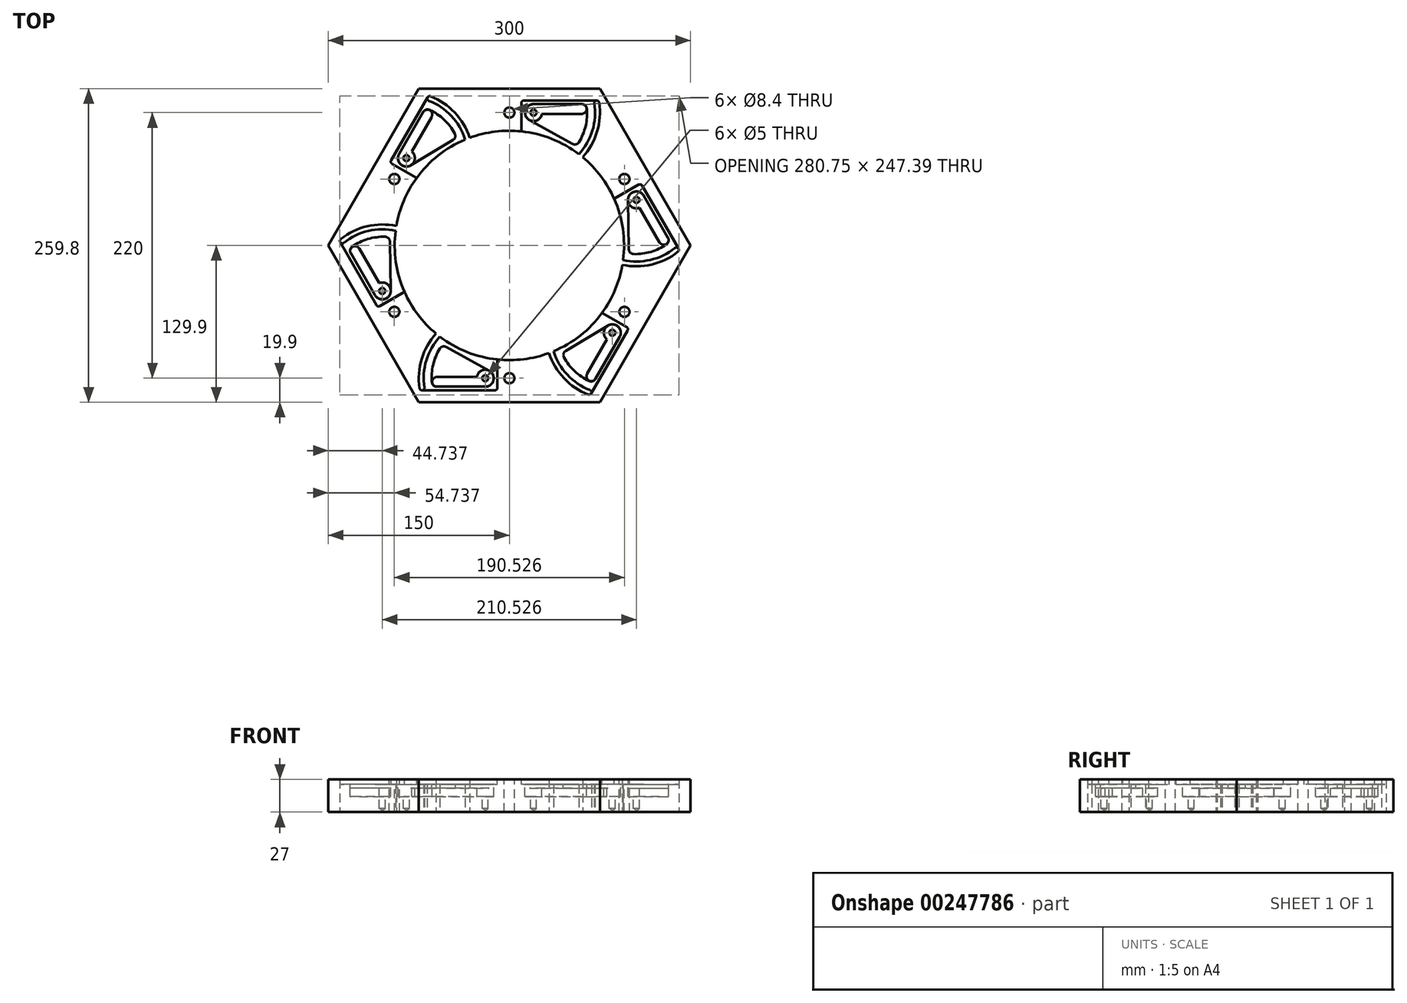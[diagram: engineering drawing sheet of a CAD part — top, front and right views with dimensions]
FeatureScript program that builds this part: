
annotation { "Feature Type Name" : "Feature", "Feature Type Description" : "" }
export const myFeature = defineFeature(function(context is Context, id is Id, definition is map)
    precondition{}
    {
        {
            var Q0;
            Q0=qCreatedBy(makeId("Top.planeOp"),FACE);
            var sketch = newSketch(context, id + "F0", { "sketchPlane" : qUnion([Q0])});
            skCircle(sketch, "E0.cCircle", {"center": v(0, 0) * mm, "radius": 150 * mm, "construction": true});
            skLineSegment(sketch, "E0.0", {"start": v(-75, 129.9) * mm, "end": v(75, 129.9) * mm});
            skLineSegment(sketch, "E0.1", {"start": v(75, 129.9) * mm, "end": v(150, 0) * mm});
            skLineSegment(sketch, "E0.2", {"start": v(150, 0) * mm, "end": v(75, -129.9) * mm});
            skLineSegment(sketch, "E0.3", {"start": v(75, -129.9) * mm, "end": v(-75, -129.9) * mm});
            skLineSegment(sketch, "E0.4", {"start": v(-75, -129.9) * mm, "end": v(-150, 0) * mm});
            skLineSegment(sketch, "E0.5", {"start": v(-150, 0) * mm, "end": v(-75, 129.9) * mm});
            skCircle(sketch, "E1", {"center": v(0, 0) * mm, "radius": 95 * mm});
            skLineSegment(sketch, "E2", {"start": v(0, -192.57) * mm, "end": v(0, 170.24) * mm, "construction": true});
            skCircle(sketch, "E3", {"center": v(0, 0) * mm, "radius": 110 * mm, "construction": true});
            skCircle(sketch, "E4", {"center": v(0, 110) * mm, "radius": 4.2 * mm});
            skCircle(sketch, "E5.1.0", {"center": v(-95.26, 55) * mm, "radius": 4.2 * mm});
            skCircle(sketch, "E5.2.0", {"center": v(-95.26, -55) * mm, "radius": 4.2 * mm});
            skCircle(sketch, "E5.3.0", {"center": v(0, -110) * mm, "radius": 4.2 * mm});
            skCircle(sketch, "E5.4.0", {"center": v(95.26, -55) * mm, "radius": 4.2 * mm});
            skCircle(sketch, "E5.5.0", {"center": v(95.26, 55) * mm, "radius": 4.2 * mm});
            skSolve(sketch);
        }
        {
            var Q0;
            Q0=qSketchRegion(id+"F0",true);
            extrude(context, id + "F1", {"entities" : qUnion([Q0]), "oppositeDirection" : true, "depth" : 25 * mm, "hasSecondDirection" : true, "secondDirectionOppositeDirection" : false, "secondDirectionDepth" : 2 * mm});
        }
        {
            var Q0;
            Q0=qCreatedBy(makeId("Top.planeOp"),FACE);
            var sketch = newSketch(context, id + "F2", { "sketchPlane" : qUnion([Q0])});
            skLineSegment(sketch, "E6", {"start": v(0, 0) * mm, "end": v(-115.33, 66.59) * mm, "construction": true});
            skLineSegment(sketch, "E7", {"start": v(24.73, 8.82) * mm, "end": v(-118.6, 91.57) * mm, "construction": true});
            skLineSegment(sketch, "E8", {"start": v(-73.53, 92.65) * mm, "end": v(-110.35, 28.87) * mm, "construction": true});
            skPoint(sketch, "E9", {"position": v(-85.26, 72.32) * mm});
            skArc(sketch, "E10", {"start": v(-79.2, 122.96) * mm, "mid": v(-97.67, 22.85) * mm, "end": v(-66.72, 119.83) * mm, "construction": true});
            skArc(sketch, "E11", {"start": v(-78.72, 126.93) * mm, "mid": v(-131.29, 42.21) * mm, "end": v(-32.6, 56.43) * mm});
            skCircle(sketch, "E12", {"center": v(-85.26, 72.32) * mm, "radius": 2.5 * mm, "construction": true});
            skArc(sketch, "E13", {"start": v(-86.7, 77.1) * mm, "mid": v(-89.8, 70.21) * mm, "end": v(-82.54, 68.13) * mm, "construction": true});
            skLineSegment(sketch, "E14", {"start": v(-95.36, 62.49) * mm, "end": v(-73.35, 109.7) * mm, "construction": true});
            skArc(sketch, "E15", {"start": v(-86.7, 77.1) * mm, "mid": v(-83.05, 79.12) * mm, "end": v(-80.54, 82.45) * mm, "construction": true});
            skLineSegment(sketch, "E16.trimOffspring", {"start": v(-80.54, 82.45) * mm, "end": v(-62.02, 122.17) * mm, "construction": true});
            skLineSegment(sketch, "E17.trimOffspring", {"start": v(-37.22, 89.44) * mm, "end": v(-33.46, 90.8) * mm});
            skPoint(sketch, "E18", {"position": v(-62.02, 122.17) * mm});
            skPoint(sketch, "E19", {"position": v(-33.46, 90.8) * mm});
            skArc(sketch, "E20", {"start": v(-37.22, 89.44) * mm, "mid": v(-37.91, 91.27) * mm, "end": v(-38.67, 93.07) * mm});
            skLineSegment(sketch, "E21", {"start": v(-82.54, 68.13) * mm, "end": v(-42.49, 94.14) * mm, "construction": true});
            skLineSegment(sketch, "E22", {"start": v(-50.7, 85.23) * mm, "end": v(-31.42, 97.75) * mm, "construction": true});
            skPoint(sketch, "E23", {"position": v(-39.97, 95.77) * mm});
            skCircle(sketch, "E24", {"center": v(-39.97, 95.77) * mm, "radius": 3 * mm, "construction": true});
            skPoint(sketch, "E25", {"position": v(-42.49, 94.14) * mm});
            skArc(sketch, "E26.trimOffspring", {"start": v(-39.97, 95.77) * mm, "mid": v(-49.96, 109.12) * mm, "end": v(-63.7, 118.54) * mm, "construction": true});
            skLineSegment(sketch, "E27.trimOffspring", {"start": v(-39.97, 95.77) * mm, "end": v(-16, 111.34) * mm});
            skArc(sketch, "E28", {"start": v(-38.67, 93.07) * mm, "mid": v(-40.33, 94.5) * mm, "end": v(-42.49, 94.14) * mm});
            skPoint(sketch, "E29", {"position": v(-77.2, 132.91) * mm});
            skPoint(sketch, "E30", {"position": v(-78.72, 126.93) * mm});
            skLineSegment(sketch, "E31", {"start": v(-85.26, 72.32) * mm, "end": v(-78.72, 126.93) * mm, "construction": true});
            skLineSegment(sketch, "E32", {"start": v(-85.21, 72.2) * mm, "end": v(-33.46, 90.8) * mm, "construction": true});
            skPoint(sketch, "E33", {"position": v(-56.33, 130.09) * mm});
            skLineSegment(sketch, "E34", {"start": v(-97.92, 70.4) * mm, "end": v(-67.73, 122.7) * mm});
            skLineSegment(sketch, "E35.1.0", {"start": v(0, 0) * mm, "end": v(-115.33, -66.59) * mm});
            skPoint(sketch, "E35.1.1", {"position": v(-105.26, -37.68) * mm});
            skLineSegment(sketch, "E35.2.0", {"start": v(0, 0) * mm, "end": v(0, -133.17) * mm});
            skPoint(sketch, "E35.2.1", {"position": v(-20, -110) * mm});
            skLineSegment(sketch, "E35.3.0", {"start": v(0, 0) * mm, "end": v(115.33, -66.59) * mm});
            skPoint(sketch, "E35.3.1", {"position": v(85.26, -72.32) * mm});
            skLineSegment(sketch, "E35.4.0", {"start": v(0, 0) * mm, "end": v(115.33, 66.59) * mm});
            skPoint(sketch, "E35.4.1", {"position": v(105.26, 37.68) * mm});
            skLineSegment(sketch, "E35.5.0", {"start": v(0, 0) * mm, "end": v(0, 133.17) * mm});
            skPoint(sketch, "E35.5.1", {"position": v(20, 110) * mm});
            skPoint(sketch, "E35.center", {"position": v(0, 0) * mm});
            skCircle(sketch, "E36.0", {"center": v(0, 0) * mm, "radius": 95 * mm, "construction": true});
            skPoint(sketch, "E37", {"position": v(-32.9, 89.12) * mm});
            skLineSegment(sketch, "E38", {"start": v(-32.9, 89.12) * mm, "end": v(32.9, -89.12) * mm, "construction": true});
            skPoint(sketch, "E39", {"position": v(-22.5, 60.98) * mm});
            skPoint(sketch, "E40", {"position": v(5.2, -14.07) * mm});
            skCircle(sketch, "E41", {"center": v(5.2, -14.07) * mm, "radius": 80 * mm, "construction": true});
            skArc(sketch, "E42.filletArc", {"start": v(-65.27, 123.56) * mm, "mid": v(-66.66, 123.58) * mm, "end": v(-67.73, 122.7) * mm});
            skLineSegment(sketch, "E43", {"start": v(-32.6, 56.43) * mm, "end": v(-85.26, 72.32) * mm, "construction": true});
            skLineSegment(sketch, "E44", {"start": v(-76.12, 72.3) * mm, "end": v(-85.21, 72.2) * mm});
            skLineSegment(sketch, "E45", {"start": v(-85.21, 72.2) * mm, "end": v(-56.33, 90.95) * mm, "construction": true});
            skLineSegment(sketch, "E46", {"start": v(-85.21, 72.2) * mm, "end": v(-48.78, 69.91) * mm, "construction": true});
            skLineSegment(sketch, "E47", {"start": v(-48.77, 65.04) * mm, "end": v(-92.23, 67.76) * mm, "construction": true});
            skCircle(sketch, "E48", {"center": v(-85.21, 72.2) * mm, "radius": 10 * mm, "construction": true});
            skLineSegment(sketch, "E49", {"start": v(-87.5, 62.45) * mm, "end": v(-55.32, 60.44) * mm, "construction": true});
            skLineSegment(sketch, "E50", {"start": v(-97.2, 67.66) * mm, "end": v(-68.1, 50.87) * mm});
            skArc(sketch, "E51.filletArc", {"start": v(-97.92, 70.4) * mm, "mid": v(-98.12, 68.87) * mm, "end": v(-97.2, 67.66) * mm});
            skArc(sketch, "E52", {"start": v(-67.73, 122.7) * mm, "mid": v(-67.88, 121.03) * mm, "end": v(-66.72, 119.83) * mm, "construction": true});
            skArc(sketch, "E53.converted", {"start": v(-30.7, 79.26) * mm, "mid": v(-41.9, 106.16) * mm, "end": v(-65.27, 123.56) * mm});
            skArc(sketch, "E54", {"start": v(-30.7, 79.26) * mm, "mid": v(-51.4, 67.7) * mm, "end": v(-68.1, 50.87) * mm});
            skLineSegment(sketch, "E55.trimOffspring", {"start": v(-52.18, 41.68) * mm, "end": v(-31.82, 29.92) * mm});
            skSolve(sketch);
        }
        {
            var Q0;
            Q0=qCreatedBy(makeId("Front.planeOp"),FACE);
            var sketch = newSketch(context, id + "F3", { "sketchPlane" : qUnion([Q0])});
            skLineSegment(sketch, "E56", {"start": v(0, -93.36) * mm, "end": v(0, 93) * mm, "construction": true});
            skSolve(sketch);
        }
        {
            var Q0;
            Q0=qSketchRegion(id+"F2",true);
            extrude(context, id + "F4", {"entities" : qUnion([Q0]), "depth" : 25 * mm, "hasSecondDirection" : true, "secondDirectionOppositeDirection" : true, "secondDirectionDepth" : 2.1 * mm});
        }
        {
            var Q0;
            Q0=makeQuery(id+"F4.opExtrude","SWEPT_BODY",BODY,{"disambiguationData":[OSD([sQuery(id+"F2.wireOp",EDGE,"E34"),sQuery(id+"F2.wireOp",EDGE,"E42.filletArc"),sQuery(id+"F2.wireOp",EDGE,"E50"),sQuery(id+"F2.wireOp",EDGE,"E51.filletArc"),sQuery(id+"F2.wireOp",EDGE,"E54"),sQuery(id+"F2.wireOp",EDGE,"E53.converted")])]});
            var Q1;
            Q1=sQuery(id+"F3.wireOp",EDGE,"E56");
            circularPattern(context, id + "F5", {"entities" : qUnion([Q0]), "axis" : qUnion([Q1]), "angle" : 360 * degree, "instanceCount" : 6, "equalSpace" : true});
        }
        {
            var Q0;
            Q0=makeQuery(id+"F5.opPattern","COPY",BODY,{"derivedFrom":makeQuery(id+"F4.opExtrude","SWEPT_BODY",BODY,{"disambiguationData":[OSD([sQuery(id+"F2.wireOp",EDGE,"E34"),sQuery(id+"F2.wireOp",EDGE,"E42.filletArc"),sQuery(id+"F2.wireOp",EDGE,"E50"),sQuery(id+"F2.wireOp",EDGE,"E51.filletArc"),sQuery(id+"F2.wireOp",EDGE,"E54"),sQuery(id+"F2.wireOp",EDGE,"E53.converted")])]}),"instanceName":"1"});
            var Q1;
            Q1=makeQuery(id+"F4.opExtrude","SWEPT_BODY",BODY,{"disambiguationData":[OSD([sQuery(id+"F2.wireOp",EDGE,"E34"),sQuery(id+"F2.wireOp",EDGE,"E42.filletArc"),sQuery(id+"F2.wireOp",EDGE,"E50"),sQuery(id+"F2.wireOp",EDGE,"E51.filletArc"),sQuery(id+"F2.wireOp",EDGE,"E54"),sQuery(id+"F2.wireOp",EDGE,"E53.converted")])]});
            var Q2;
            Q2=makeQuery(id+"F5.opPattern","COPY",BODY,{"derivedFrom":makeQuery(id+"F4.opExtrude","SWEPT_BODY",BODY,{"disambiguationData":[OSD([sQuery(id+"F2.wireOp",EDGE,"E34"),sQuery(id+"F2.wireOp",EDGE,"E42.filletArc"),sQuery(id+"F2.wireOp",EDGE,"E50"),sQuery(id+"F2.wireOp",EDGE,"E51.filletArc"),sQuery(id+"F2.wireOp",EDGE,"E54"),sQuery(id+"F2.wireOp",EDGE,"E53.converted")])]}),"instanceName":"5"});
            var Q3;
            Q3=makeQuery(id+"F5.opPattern","COPY",BODY,{"derivedFrom":makeQuery(id+"F4.opExtrude","SWEPT_BODY",BODY,{"disambiguationData":[OSD([sQuery(id+"F2.wireOp",EDGE,"E34"),sQuery(id+"F2.wireOp",EDGE,"E42.filletArc"),sQuery(id+"F2.wireOp",EDGE,"E50"),sQuery(id+"F2.wireOp",EDGE,"E51.filletArc"),sQuery(id+"F2.wireOp",EDGE,"E54"),sQuery(id+"F2.wireOp",EDGE,"E53.converted")])]}),"instanceName":"4"});
            var Q4;
            Q4=makeQuery(id+"F5.opPattern","COPY",BODY,{"derivedFrom":makeQuery(id+"F4.opExtrude","SWEPT_BODY",BODY,{"disambiguationData":[OSD([sQuery(id+"F2.wireOp",EDGE,"E34"),sQuery(id+"F2.wireOp",EDGE,"E42.filletArc"),sQuery(id+"F2.wireOp",EDGE,"E50"),sQuery(id+"F2.wireOp",EDGE,"E51.filletArc"),sQuery(id+"F2.wireOp",EDGE,"E54"),sQuery(id+"F2.wireOp",EDGE,"E53.converted")])]}),"instanceName":"3"});
            var Q5;
            Q5=makeQuery(id+"F5.opPattern","COPY",BODY,{"derivedFrom":makeQuery(id+"F4.opExtrude","SWEPT_BODY",BODY,{"disambiguationData":[OSD([sQuery(id+"F2.wireOp",EDGE,"E34"),sQuery(id+"F2.wireOp",EDGE,"E42.filletArc"),sQuery(id+"F2.wireOp",EDGE,"E50"),sQuery(id+"F2.wireOp",EDGE,"E51.filletArc"),sQuery(id+"F2.wireOp",EDGE,"E54"),sQuery(id+"F2.wireOp",EDGE,"E53.converted")])]}),"instanceName":"2"});
            var Q6;
            Q6=makeQuery(id+"F1.opExtrude","SWEPT_BODY",BODY,{"disambiguationData":[OSD([sQuery(id+"F0.wireOp",EDGE,"E0.0"),sQuery(id+"F0.wireOp",EDGE,"E0.1"),sQuery(id+"F0.wireOp",EDGE,"E0.2"),sQuery(id+"F0.wireOp",EDGE,"E0.3"),sQuery(id+"F0.wireOp",EDGE,"E0.4"),sQuery(id+"F0.wireOp",EDGE,"E0.5"),sQuery(id+"F0.wireOp",EDGE,"E1")])]});
            booleanBodies(context, id + "F6", {"operationType" : BooleanOperationType.SUBTRACTION, "tools" : qUnion([Q0, Q1, Q2, Q3, Q4, Q5]), "targets" : qUnion([Q6])});
        }
        {
            var Q0;
            Q0=makeQuery(id+"F0.imprint","IMPRINT",FACE,{"disambiguationData":[TD([[makeQuery(id+"F0.imprint","IMPRINT",EDGE,{"derivedFrom":sQuery(id+"F0.wireOp",EDGE,"E1")}),1.0]])]});
            var sketch = newSketch(context, id + "F7", { "sketchPlane" : qUnion([Q0])});
            skArc(sketch, "E57.1", {"start": v(-34.54, 77.66) * mm, "mid": v(-44.72, 103.26) * mm, "end": v(-66.72, 119.83) * mm});
            skArc(sketch, "E58.0", {"start": v(-30.7, 79.26) * mm, "mid": v(-32.63, 78.49) * mm, "end": v(-34.54, 77.66) * mm});
            skArc(sketch, "E59.0", {"start": v(-67.73, 122.7) * mm, "mid": v(-67.88, 121.03) * mm, "end": v(-66.72, 119.83) * mm});
            skArc(sketch, "E59.1", {"start": v(-65.27, 123.56) * mm, "mid": v(-66.66, 123.58) * mm, "end": v(-67.73, 122.7) * mm});
            skArc(sketch, "E59.2", {"start": v(-30.7, 79.26) * mm, "mid": v(-41.9, 106.16) * mm, "end": v(-65.27, 123.56) * mm});
            skPoint(sketch, "E60.orphan", {"position": v(-68.1, 50.87) * mm});
            skPoint(sketch, "E61.orphan", {"position": v(-79.2, 122.96) * mm});
            skPoint(sketch, "E57.0.end.orphan", {"position": v(-97.92, 70.4) * mm});
            skPoint(sketch, "E57.0.start.orphan", {"position": v(-67.73, 122.7) * mm});
            skSolve(sketch);
        }
        {
            var Q0;
            Q0=qSketchRegion(id+"F7",true);
            extrude(context, id + "F8", {"entities" : qUnion([Q0]), "depth" : 10 * mm, "hasSecondDirection" : true, "secondDirectionOppositeDirection" : true, "secondDirectionDepth" : 35 * mm});
        }
        {
            var Q0;
            Q0=makeQuery(id+"F8.opExtrude","SWEPT_BODY",BODY,{"disambiguationData":[OSD([sQuery(id+"F7.wireOp",EDGE,"E57.1"),sQuery(id+"F7.wireOp",EDGE,"E58.0"),sQuery(id+"F7.wireOp",EDGE,"E59.0"),sQuery(id+"F7.wireOp",EDGE,"E59.1"),sQuery(id+"F7.wireOp",EDGE,"E59.2")])]});
            var Q1;
            Q1=sQuery(id+"F3.wireOp",EDGE,"E56");
            circularPattern(context, id + "F9", {"entities" : qUnion([Q0]), "axis" : qUnion([Q1]), "angle" : 360 * degree, "instanceCount" : 6, "equalSpace" : true});
        }
        {
            var Q0;
            Q0=makeQuery(id+"F8.opExtrude","SWEPT_BODY",BODY,{"disambiguationData":[OSD([sQuery(id+"F7.wireOp",EDGE,"E57.1"),sQuery(id+"F7.wireOp",EDGE,"E58.0"),sQuery(id+"F7.wireOp",EDGE,"E59.0"),sQuery(id+"F7.wireOp",EDGE,"E59.1"),sQuery(id+"F7.wireOp",EDGE,"E59.2")])]});
            var Q1;
            Q1=makeQuery(id+"F9.opPattern","COPY",BODY,{"derivedFrom":makeQuery(id+"F8.opExtrude","SWEPT_BODY",BODY,{"disambiguationData":[OSD([sQuery(id+"F7.wireOp",EDGE,"E57.1"),sQuery(id+"F7.wireOp",EDGE,"E58.0"),sQuery(id+"F7.wireOp",EDGE,"E59.0"),sQuery(id+"F7.wireOp",EDGE,"E59.1"),sQuery(id+"F7.wireOp",EDGE,"E59.2")])]}),"instanceName":"5"});
            var Q2;
            Q2=makeQuery(id+"F9.opPattern","COPY",BODY,{"derivedFrom":makeQuery(id+"F8.opExtrude","SWEPT_BODY",BODY,{"disambiguationData":[OSD([sQuery(id+"F7.wireOp",EDGE,"E57.1"),sQuery(id+"F7.wireOp",EDGE,"E58.0"),sQuery(id+"F7.wireOp",EDGE,"E59.0"),sQuery(id+"F7.wireOp",EDGE,"E59.1"),sQuery(id+"F7.wireOp",EDGE,"E59.2")])]}),"instanceName":"4"});
            var Q3;
            Q3=makeQuery(id+"F9.opPattern","COPY",BODY,{"derivedFrom":makeQuery(id+"F8.opExtrude","SWEPT_BODY",BODY,{"disambiguationData":[OSD([sQuery(id+"F7.wireOp",EDGE,"E57.1"),sQuery(id+"F7.wireOp",EDGE,"E58.0"),sQuery(id+"F7.wireOp",EDGE,"E59.0"),sQuery(id+"F7.wireOp",EDGE,"E59.1"),sQuery(id+"F7.wireOp",EDGE,"E59.2")])]}),"instanceName":"3"});
            var Q4;
            Q4=makeQuery(id+"F9.opPattern","COPY",BODY,{"derivedFrom":makeQuery(id+"F8.opExtrude","SWEPT_BODY",BODY,{"disambiguationData":[OSD([sQuery(id+"F7.wireOp",EDGE,"E57.1"),sQuery(id+"F7.wireOp",EDGE,"E58.0"),sQuery(id+"F7.wireOp",EDGE,"E59.0"),sQuery(id+"F7.wireOp",EDGE,"E59.1"),sQuery(id+"F7.wireOp",EDGE,"E59.2")])]}),"instanceName":"2"});
            var Q5;
            Q5=makeQuery(id+"F9.opPattern","COPY",BODY,{"derivedFrom":makeQuery(id+"F8.opExtrude","SWEPT_BODY",BODY,{"disambiguationData":[OSD([sQuery(id+"F7.wireOp",EDGE,"E57.1"),sQuery(id+"F7.wireOp",EDGE,"E58.0"),sQuery(id+"F7.wireOp",EDGE,"E59.0"),sQuery(id+"F7.wireOp",EDGE,"E59.1"),sQuery(id+"F7.wireOp",EDGE,"E59.2")])]}),"instanceName":"1"});
            var Q6;
            Q6=makeQuery(id+"F1.opExtrude","SWEPT_BODY",BODY,{"disambiguationData":[OSD([sQuery(id+"F0.wireOp",EDGE,"E0.0"),sQuery(id+"F0.wireOp",EDGE,"E0.1"),sQuery(id+"F0.wireOp",EDGE,"E0.2"),sQuery(id+"F0.wireOp",EDGE,"E0.3"),sQuery(id+"F0.wireOp",EDGE,"E0.4"),sQuery(id+"F0.wireOp",EDGE,"E0.5"),sQuery(id+"F0.wireOp",EDGE,"E1")])]});
            booleanBodies(context, id + "F10", {"operationType" : BooleanOperationType.SUBTRACTION, "tools" : qUnion([Q0, Q1, Q2, Q3, Q4, Q5]), "targets" : qUnion([Q6])});
        }
        {
            var Q0;
            Q0=sQuery(id+"F2.wireOp",VERTEX,"E35.5.1");
            var Q1;
            Q1=sQuery(id+"F2.wireOp",VERTEX,"E35.4.1");
            var Q2;
            Q2=sQuery(id+"F2.wireOp",VERTEX,"E35.3.1");
            var Q3;
            Q3=sQuery(id+"F2.wireOp",VERTEX,"E35.2.1");
            var Q4;
            Q4=sQuery(id+"F2.wireOp",VERTEX,"E35.1.1");
            var Q5;
            Q5=sQuery(id+"F2.wireOp",VERTEX,"E9");
            var Q6;
            Q6=makeQuery(id+"F1.opExtrude","SWEPT_BODY",BODY,{"disambiguationData":[OSD([sQuery(id+"F0.wireOp",EDGE,"E0.0"),sQuery(id+"F0.wireOp",EDGE,"E0.1"),sQuery(id+"F0.wireOp",EDGE,"E0.2"),sQuery(id+"F0.wireOp",EDGE,"E0.3"),sQuery(id+"F0.wireOp",EDGE,"E0.4"),sQuery(id+"F0.wireOp",EDGE,"E0.5"),sQuery(id+"F0.wireOp",EDGE,"E1")])]});
            hole(context, id + "F11", {"style" : HoleStyle.SIMPLE, "endStyle" : HoleEndStyle.BLIND, "holeDiameter" : 5 * mm, "holeDepth" : 20 * mm, "locations" : qUnion([Q0, Q1, Q2, Q3, Q4, Q5]), "scope" : qUnion([Q6])});
        }
        {
            var Q0;
            Q0=makeQuery(id+"F6.opBoolean","COPY",FACE,{"derivedFrom":makeQuery(id+"F4.opExtrude","CAP_FACE",FACE,{"disambiguationData":[OSD([sQuery(id+"F2.wireOp",EDGE,"E34"),sQuery(id+"F2.wireOp",EDGE,"E42.filletArc"),sQuery(id+"F2.wireOp",EDGE,"E50"),sQuery(id+"F2.wireOp",EDGE,"E51.filletArc"),sQuery(id+"F2.wireOp",EDGE,"E54"),sQuery(id+"F2.wireOp",EDGE,"E53.converted")])],"isStart":true})});
            cPlane(context, id + "F12", {"entities" : qUnion([Q0]), "cplaneType" : CPlaneType.OFFSET, "offset" : 0 * mm, "width" : 150 * mm, "height" : 150 * mm});
        }
        {
            var Q0;
            Q0=qCreatedBy(id+"F12.planeOp",FACE);
            var sketch = newSketch(context, id + "F13", { "sketchPlane" : qUnion([Q0])});
            skCircle(sketch, "E62.0", {"center": v(-85.26, 72.32) * mm, "radius": 7 * mm});
            skLineSegment(sketch, "E63", {"start": v(-91.32, 75.82) * mm, "end": v(-67.64, 116.85) * mm});
            skLineSegment(sketch, "E64", {"start": v(-87.86, 73.82) * mm, "end": v(-63.58, 115.87) * mm, "construction": true});
            skLineSegment(sketch, "E65", {"start": v(-91.32, 75.82) * mm, "end": v(-76.61, 67.33) * mm, "construction": true});
            skLineSegment(sketch, "E66", {"start": v(-77.1, 113.8) * mm, "end": v(-55.5, 101.33) * mm, "construction": true});
            skArc(sketch, "E67", {"start": v(-64.4, 106.46) * mm, "mid": v(-65.86, 111.93) * mm, "end": v(-71.32, 110.46) * mm});
            skArc(sketch, "E68", {"start": v(-91.32, 75.82) * mm, "mid": v(-89.86, 70.36) * mm, "end": v(-84.4, 71.82) * mm});
            skLineSegment(sketch, "E69", {"start": v(-64.4, 106.46) * mm, "end": v(-84.4, 71.82) * mm});
            skSolve(sketch);
        }
        {
            var Q0;
            Q0=qSketchRegion(id+"F13",true);
            extrude(context, id + "F14", {"entities" : qUnion([Q0]), "oppositeDirection" : true, "depth" : 10 * mm, "hasSecondDirection" : true, "secondDirectionOppositeDirection" : false, "secondDirectionDepth" : 25 * mm});
        }
        {
            var Q0;
            Q0=makeQuery(id+"F14.opExtrude","SWEPT_BODY",BODY,{"disambiguationData":[OSD([sQuery(id+"F13.wireOp",EDGE,"E62.0")])]});
            var Q1;
            Q1=sQuery(id+"F3.wireOp",EDGE,"E56");
            circularPattern(context, id + "F15", {"operationType" : NewBodyOperationType.REMOVE, "entities" : qUnion([Q0]), "axis" : qUnion([Q1]), "angle" : 360 * degree, "instanceCount" : 6, "equalSpace" : true});
        }
        {
            var Q0;
            Q0=qCreatedBy(id+"F12.planeOp",FACE);
            var sketch = newSketch(context, id + "F16", { "sketchPlane" : qUnion([Q0])});
            skArc(sketch, "E70.0", {"start": v(-66.31, 118.88) * mm, "mid": v(-47.6, 106.21) * mm, "end": v(-36.21, 86.7) * mm, "construction": true});
            skCircle(sketch, "E71.0", {"center": v(-85.26, 72.32) * mm, "radius": 4.5 * mm, "construction": true});
            skLineSegment(sketch, "E72.0", {"start": v(-67.73, 122.7) * mm, "end": v(-103.72, 60.35) * mm, "construction": true});
            skArc(sketch, "E73.0", {"start": v(-76.82, 55.9) * mm, "mid": v(-58.9, 74.54) * mm, "end": v(-36.62, 87.66) * mm, "construction": true});
            skArc(sketch, "E74", {"start": v(-45.23, 92.65) * mm, "mid": v(-54.06, 104.16) * mm, "end": v(-66.1, 112.27) * mm});
            skPoint(sketch, "E75.orphan", {"position": v(-61.95, 122.7) * mm});
            skArc(sketch, "E76.0.0", {"start": v(-91.32, 75.82) * mm, "mid": v(-90.17, 67.33) * mm, "end": v(-81.66, 66.32) * mm});
            skLineSegment(sketch, "E77", {"start": v(-91.32, 75.82) * mm, "end": v(-71.23, 110.63) * mm});
            skLineSegment(sketch, "E78", {"start": v(-46.7, 87.33) * mm, "end": v(-81.66, 66.32) * mm});
            skPoint(sketch, "E79.visualSharp", {"position": v(-69.48, 113.66) * mm});
            skArc(sketch, "E79.filletArc", {"start": v(-66.1, 112.27) * mm, "mid": v(-68.97, 112.45) * mm, "end": v(-71.23, 110.63) * mm});
            skPoint(sketch, "E80.visualSharp", {"position": v(-43.57, 89.2) * mm});
            skArc(sketch, "E80.filletArc", {"start": v(-46.7, 87.33) * mm, "mid": v(-44.9, 89.7) * mm, "end": v(-45.23, 92.65) * mm});
            skSolve(sketch);
        }
        {
            var Q0;
            Q0=qSketchRegion(id+"F16",true);
            extrude(context, id + "F17", {"entities" : qUnion([Q0]), "oppositeDirection" : true, "depth" : 3 * mm, "hasSecondDirection" : true, "secondDirectionOppositeDirection" : false, "secondDirectionDepth" : 25 * mm});
        }
        {
            var Q0;
            Q0=makeQuery(id+"F17.opExtrude","SWEPT_BODY",BODY,{"disambiguationData":[OSD([sQuery(id+"F16.wireOp",EDGE,"E74"),sQuery(id+"F16.wireOp",EDGE,"E76.0.0"),sQuery(id+"F16.wireOp",EDGE,"E77"),sQuery(id+"F16.wireOp",EDGE,"E78"),sQuery(id+"F16.wireOp",EDGE,"E79.filletArc"),sQuery(id+"F16.wireOp",EDGE,"E80.filletArc")])]});
            var Q1;
            Q1=sQuery(id+"F3.wireOp",EDGE,"E56");
            circularPattern(context, id + "F18", {"operationType" : NewBodyOperationType.REMOVE, "entities" : qUnion([Q0]), "axis" : qUnion([Q1]), "angle" : 360 * degree, "instanceCount" : 6, "oppositeDirection" : true, "equalSpace" : true});
        }
    });
